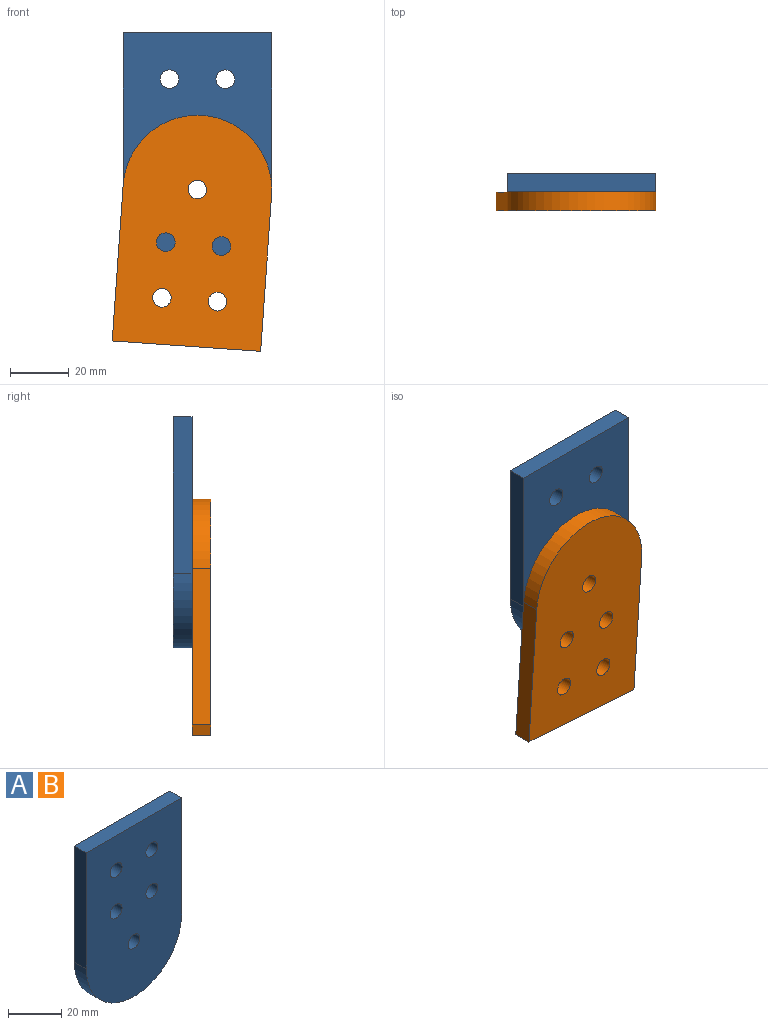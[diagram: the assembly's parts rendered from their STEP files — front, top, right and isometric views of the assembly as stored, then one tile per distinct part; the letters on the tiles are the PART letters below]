
ASSEMBLY  parts=2 mates=1
PART A: 11 faces, bbox 50.8x6.4x79 mm
  f0: cylinder r=25.4mm len=50.8mm, axis (0,1,0), area 506.7mm2, adj f1,f7,f9,f10
  f1: plane 53.59x6.35mm, normal (1,0,0), area 340.3mm2, adj f0,f2,f9,f10
  f2: plane 50.8x6.35mm, normal (0,0,1), area 322.6mm2, adj f1,f7,f9,f10
  f3: cylinder r=3.17mm len=6.35mm, axis (0,1,0), area 126.7mm2, adj f9,f10
  f4: cylinder r=3.17mm len=6.35mm, axis (0,1,0), area 126.7mm2, adj f9,f10
  f5: cylinder r=3.17mm len=6.35mm, axis (0,1,0), area 126.7mm2, adj f9,f10
  f6: cylinder r=3.17mm len=6.35mm, axis (0,1,0), area 126.7mm2, adj f9,f10
  f7: plane 53.59x6.35mm, normal (-1,0,0), area 340.3mm2, adj f0,f2,f9,f10
  f8: cylinder r=3.17mm len=6.35mm, axis (0,1,0), area 126.7mm2, adj f9,f10
  f9: plane 78.99x50.8mm, normal (0,-1,0), area 3577.4mm2, adj f0,f1,f2,f3,f4,f5,f6,f7
  f10: plane 78.99x50.8mm, normal (0,1,0), area 3577.4mm2, adj f0,f1,f2,f3,f4,f5,f6,f7
PART B: same geometry as A
PLACE A t=(0,0,-16.34)mm
PLACE B rot(axis=(0,-1,0),176deg) t=(0,-6.35,-16.34)mm
MATE revolute A.f8 <-> B.f8  axis (0,-1,0) through (0,-6.35,-16.34)mm
